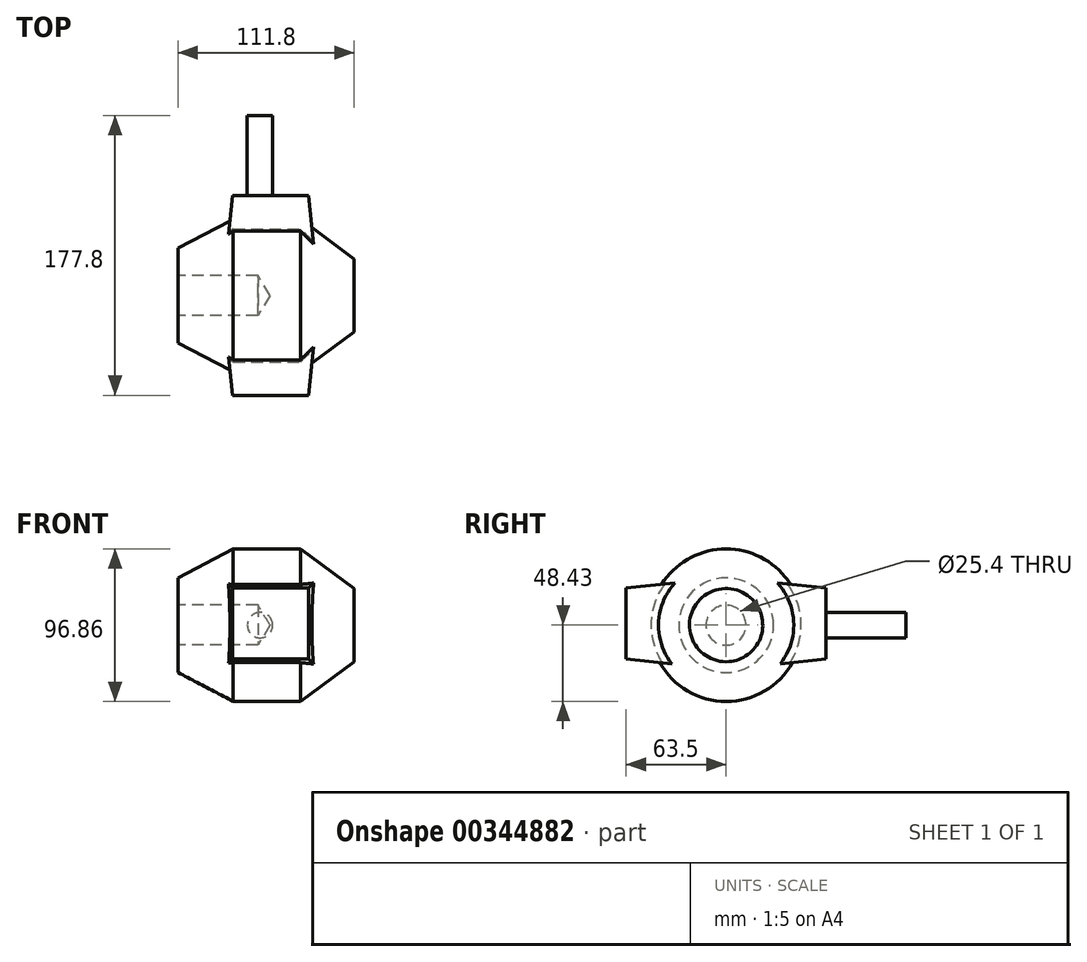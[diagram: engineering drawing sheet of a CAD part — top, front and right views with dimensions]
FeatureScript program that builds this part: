
annotation { "Feature Type Name" : "Feature", "Feature Type Description" : "" }
export const myFeature = defineFeature(function(context is Context, id is Id, definition is map)
    precondition{}
    {
        {
            var Q0;
            Q0=qCreatedBy(makeId("Front.planeOp"),FACE);
            var sketch = newSketch(context, id + "F0", { "sketchPlane" : qUnion([Q0])});
            skLineSegment(sketch, "E0.bottom", {"start": v(-24.08, 30.18) * mm, "end": v(37.5, 30.18) * mm});
            skLineSegment(sketch, "E0.top", {"start": v(-24.08, -28.23) * mm, "end": v(37.5, -28.23) * mm});
            skLineSegment(sketch, "E0.left", {"start": v(-24.08, 30.18) * mm, "end": v(-24.08, -28.23) * mm});
            skLineSegment(sketch, "E0.right", {"start": v(37.5, 30.18) * mm, "end": v(37.5, -28.23) * mm});
            skSolve(sketch);
        }
        {
            var Q0;
            Q0=makeQuery(id+"F0.imprint","IMPRINT",FACE,{"disambiguationData":[TD([[makeQuery(id+"F0.imprint","IMPRINT",EDGE,{"derivedFrom":sQuery(id+"F0.wireOp",EDGE,"E0.bottom")}),-1.0]])]});
            extrude(context, id + "F1", {"entities" : qUnion([Q0]), "oppositeDirection" : true, "depth" : 127 * mm, "hasDraft" : true, "draftAngle" : 6 * degree, "draftPullDirection" : true, "symmetric" : true});
        }
        {
            var Q0;
            Q0=makeQuery(id+"F1.opExtrude","CAP_FACE",FACE,{"disambiguationData":[OSD([sQuery(id+"F0.wireOp",EDGE,"E0.bottom"),sQuery(id+"F0.wireOp",EDGE,"E0.top"),sQuery(id+"F0.wireOp",EDGE,"E0.left"),sQuery(id+"F0.wireOp",EDGE,"E0.right")])],"isStart":false});
            var sketch = newSketch(context, id + "F2", { "sketchPlane" : qUnion([Q0])});
            skCircle(sketch, "E1", {"center": v(0, 0) * mm, "radius": 8.08 * mm});
            skSolve(sketch);
        }
        {
            var Q0;
            Q0=makeQuery(id+"F2.imprint","IMPRINT",FACE,{"disambiguationData":[TD([[makeQuery(id+"F2.imprint","IMPRINT",EDGE,{"derivedFrom":sQuery(id+"F2.wireOp",EDGE,"E1")}),1.0]])]});
            extrude(context, id + "F3", {"entities" : qUnion([Q0]), "operationType" : NewBodyOperationType.ADD, "depth" : 50.8 * mm});
        }
        {
            var Q0;
            Q0=qCreatedBy(makeId("Front.planeOp"),FACE);
            var sketch = newSketch(context, id + "F4", { "sketchPlane" : qUnion([Q0])});
            skLineSegment(sketch, "E2", {"start": v(59.74, 0) * mm, "end": v(-52.06, 0) * mm});
            skLineSegment(sketch, "E3", {"start": v(-52.06, 0) * mm, "end": v(-52.06, 30.08) * mm});
            skLineSegment(sketch, "E4", {"start": v(-52.06, 30.08) * mm, "end": v(-17.07, 48.43) * mm});
            skLineSegment(sketch, "E5", {"start": v(-17.07, 48.43) * mm, "end": v(25.6, 48.43) * mm});
            skLineSegment(sketch, "E6", {"start": v(25.6, 48.43) * mm, "end": v(59.74, 23.26) * mm});
            skLineSegment(sketch, "E7", {"start": v(59.74, 23.26) * mm, "end": v(59.74, 0) * mm});
            skSolve(sketch);
        }
        {
            var Q0;
            Q0=makeQuery(id+"F4.imprint","IMPRINT",FACE,{"disambiguationData":[TD([[makeQuery(id+"F4.imprint","IMPRINT",EDGE,{"derivedFrom":sQuery(id+"F4.wireOp",EDGE,"E2")}),-1.0]])]});
            var Q1;
            Q1=sQuery(id+"F4.wireOp",EDGE,"E2");
            revolve(context, id + "F5", {"operationType" : NewBodyOperationType.ADD, "entities" : qUnion([Q0]), "axis" : qUnion([Q1]), "revolveType" : RevolveType.FULL});
        }
        {
            var Q0;
            Q0=makeQuery(id+"F5.opRevolve","SWEPT_FACE",FACE,{"disambiguationData":[OSD([sQuery(id+"F4.wireOp",EDGE,"E3")])]});
            var sketch = newSketch(context, id + "F6", { "sketchPlane" : qUnion([Q0])});
            skPoint(sketch, "E8", {"position": v(0, 0) * mm});
            skSolve(sketch);
        }
        {
            var Q0;
            Q0=sQuery(id+"F6.wireOp",VERTEX,"E8");
            var Q1;
            Q1=makeQuery(id+"F1.*.split.splitOp","SPLIT",BODY,{"derivedFrom":makeQuery(id+"F1.opExtrude","SWEPT_BODY",BODY,{"disambiguationData":[OSD([sQuery(id+"F0.wireOp",EDGE,"E0.bottom"),sQuery(id+"F0.wireOp",EDGE,"E0.top"),sQuery(id+"F0.wireOp",EDGE,"E0.left"),sQuery(id+"F0.wireOp",EDGE,"E0.right")])]})});
            hole(context, id + "F7", {"style" : HoleStyle.SIMPLE, "endStyle" : HoleEndStyle.BLIND, "holeDiameter" : 25.4 * mm, "holeDepth" : 50.8 * mm, "isTappedThrough" : true, "tappedDepth" : 12.7 * mm, "tapClearance" : 3, "locations" : qUnion([Q0]), "scope" : qUnion([Q1])});
        }
    });
